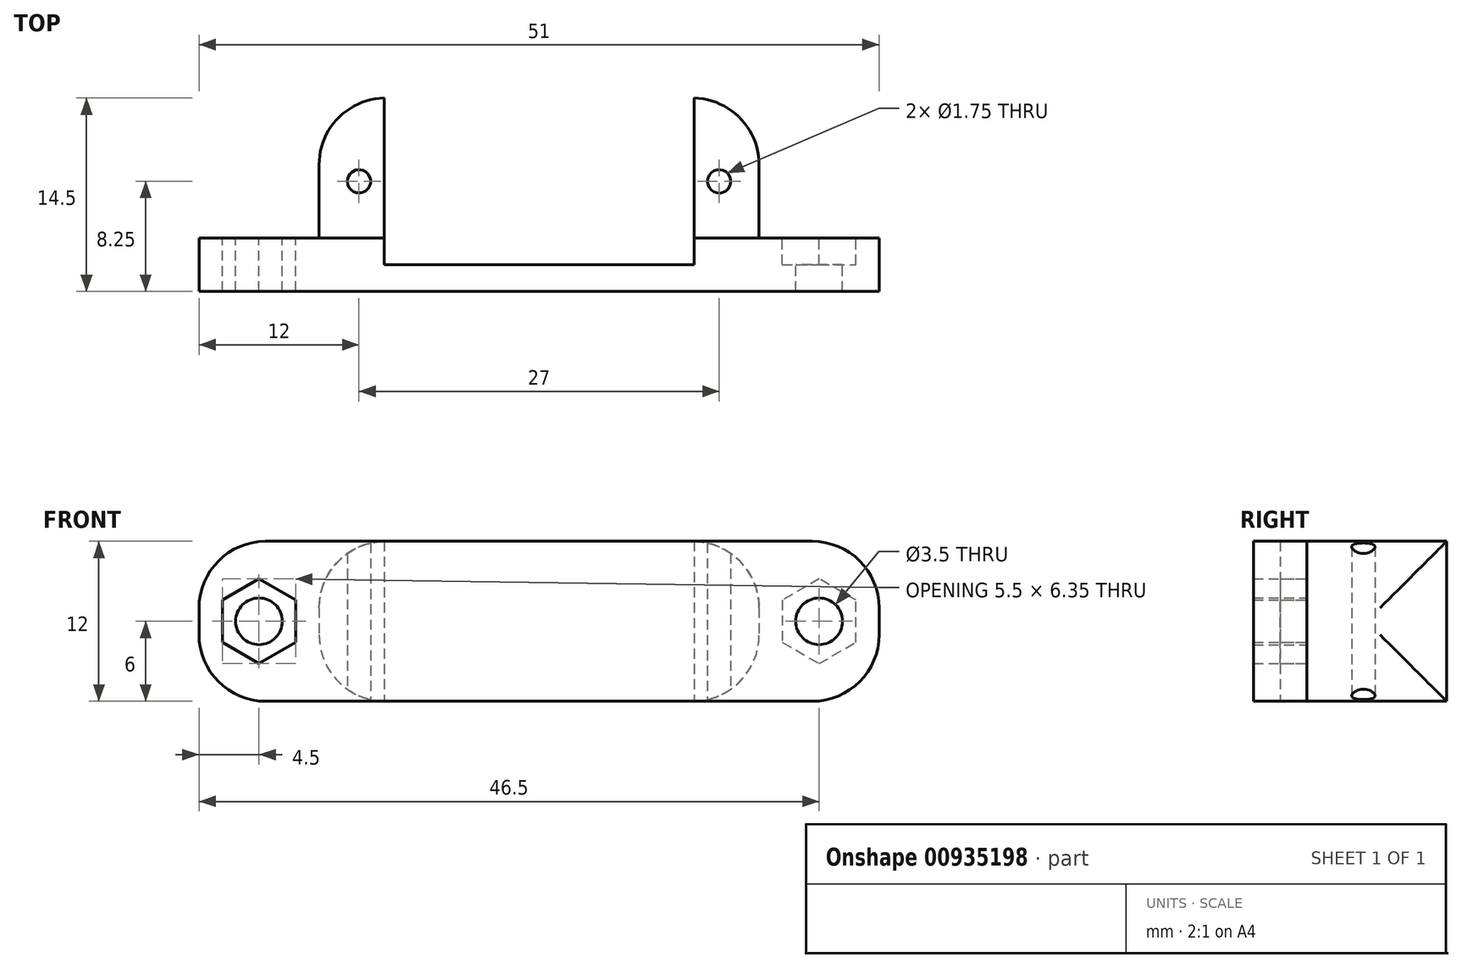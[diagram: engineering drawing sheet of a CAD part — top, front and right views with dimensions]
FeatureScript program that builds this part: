
annotation { "Feature Type Name" : "Feature", "Feature Type Description" : "" }
export const myFeature = defineFeature(function(context is Context, id is Id, definition is map)
    precondition{}
    {
        {
            var Q0;
            Q0=qCreatedBy(makeId("Top.planeOp"),FACE);
            var sketch = newSketch(context, id + "F0", { "sketchPlane" : qUnion([Q0])});
            skLineSegment(sketch, "E0.bottom", {"start": v(-16.5, 7.25) * mm, "end": v(16.5, 7.25) * mm});
            skLineSegment(sketch, "E0.top", {"start": v(-16.5, -7.25) * mm, "end": v(16.5, -7.25) * mm});
            skLineSegment(sketch, "E0.left", {"start": v(-16.5, 7.25) * mm, "end": v(-16.5, -7.25) * mm});
            skLineSegment(sketch, "E0.right", {"start": v(16.5, 7.25) * mm, "end": v(16.5, -7.25) * mm});
            skPoint(sketch, "E0.middle", {"position": v(0, 0) * mm});
            skLineSegment(sketch, "E1", {"start": v(-16.5, -5.25) * mm, "end": v(16.5, -5.25) * mm});
            skLineSegment(sketch, "E2", {"start": v(-11.63, 7.25) * mm, "end": v(-11.63, -5.25) * mm});
            skLineSegment(sketch, "E3.MirrorCS", {"start": v(11.63, 7.25) * mm, "end": v(11.63, -5.25) * mm});
            skCircle(sketch, "E4", {"center": v(-13.5, 1) * mm, "radius": 0.88 * mm});
            skCircle(sketch, "E5.MirrorC", {"center": v(13.5, 1) * mm, "radius": 0.88 * mm});
            skLineSegment(sketch, "E6.bottom", {"start": v(-16.5, -7.25) * mm, "end": v(-25.5, -7.25) * mm});
            skLineSegment(sketch, "E6.top", {"start": v(-16.5, -3.25) * mm, "end": v(-25.5, -3.25) * mm});
            skLineSegment(sketch, "E6.left", {"start": v(-16.5, -7.25) * mm, "end": v(-16.5, -3.25) * mm});
            skLineSegment(sketch, "E6.right", {"start": v(-25.5, -7.25) * mm, "end": v(-25.5, -3.25) * mm});
            skLineSegment(sketch, "E7.MirrorCS", {"start": v(16.5, -3.25) * mm, "end": v(25.5, -3.25) * mm});
            skLineSegment(sketch, "E8.MirrorCS", {"start": v(25.5, -7.25) * mm, "end": v(25.5, -3.25) * mm});
            skLineSegment(sketch, "E9.MirrorCS", {"start": v(16.5, -7.25) * mm, "end": v(25.5, -7.25) * mm});
            skSolve(sketch);
        }
        {
            var Q0;
            {var subQ3=sQuery(id+"F0.wireOp",EDGE,"E2");Q0=makeQuery(id+"F0.imprint","IMPRINT",FACE,{"disambiguationData":[TD([[makeQuery(id+"F0.imprint","IMPRINT",EDGE,{"derivedFrom":subQ3}),-1.0]])]});}
            var Q1;
            {var subQ1=sQuery(id+"F0.wireOp",EDGE,"E6.bottom");Q1=makeQuery(id+"F0.imprint","IMPRINT",FACE,{"disambiguationData":[TD([[makeQuery(id+"F0.imprint","IMPRINT",EDGE,{"derivedFrom":subQ1}),-1.0]])]});}
            var Q2;
            {var subQ1=sQuery(id+"F0.wireOp",EDGE,"E0.top");Q2=makeQuery(id+"F0.imprint","IMPRINT",FACE,{"disambiguationData":[TD([[makeQuery(id+"F0.imprint","IMPRINT",EDGE,{"derivedFrom":subQ1}),1.0]])]});}
            var Q3;
            {var subQ0=sQuery(id+"F0.wireOp",EDGE,"E7.MirrorCS");Q3=makeQuery(id+"F0.imprint","IMPRINT",FACE,{"disambiguationData":[TD([[makeQuery(id+"F0.imprint","IMPRINT",EDGE,{"derivedFrom":subQ0}),-1.0]])]});}
            var Q4;
            {var subQ4=sQuery(id+"F0.wireOp",EDGE,"E3.MirrorCS");Q4=makeQuery(id+"F0.imprint","IMPRINT",FACE,{"disambiguationData":[TD([[makeQuery(id+"F0.imprint","IMPRINT",EDGE,{"derivedFrom":subQ4}),1.0]])]});}
            extrude(context, id + "F1", {"entities" : qUnion([Q0, Q1, Q2, Q3, Q4]), "depth" : 12 * mm, "offsetDistance" : 25 * mm});
        }
        {
            var Q0;
            Q0=makeQuery(id+"F1.opExtrude","SWEPT_FACE",FACE,{"disambiguationData":[OSD([sQuery(id+"F0.wireOp",EDGE,"E7.MirrorCS")])]});
            var sketch = newSketch(context, id + "F2", { "sketchPlane" : qUnion([Q0])});
            skCircle(sketch, "E10.cCircle", {"center": v(-21, 6) * mm, "radius": 2.75 * mm, "construction": true});
            skLineSegment(sketch, "E10.0", {"start": v(-23.75, 4.41) * mm, "end": v(-23.75, 7.59) * mm});
            skLineSegment(sketch, "E10.1", {"start": v(-23.75, 7.59) * mm, "end": v(-21, 9.18) * mm});
            skLineSegment(sketch, "E10.2", {"start": v(-21, 9.18) * mm, "end": v(-18.25, 7.59) * mm});
            skLineSegment(sketch, "E10.3", {"start": v(-18.25, 7.59) * mm, "end": v(-18.25, 4.41) * mm});
            skLineSegment(sketch, "E10.4", {"start": v(-18.25, 4.41) * mm, "end": v(-21, 2.82) * mm});
            skLineSegment(sketch, "E10.5", {"start": v(-21, 2.82) * mm, "end": v(-23.75, 4.41) * mm});
            skPoint(sketch, "E10.0.midPoint", {"position": v(-23.75, 6) * mm});
            skCircle(sketch, "E11", {"center": v(-21, 6) * mm, "radius": 1.75 * mm});
            skLineSegment(sketch, "E12.MirrorCS", {"start": v(23.75, 7.59) * mm, "end": v(21, 9.18) * mm});
            skLineSegment(sketch, "E13.MirrorCS", {"start": v(21, 9.18) * mm, "end": v(18.25, 7.59) * mm});
            skLineSegment(sketch, "E14.MirrorCS", {"start": v(18.25, 4.41) * mm, "end": v(21, 2.82) * mm});
            skLineSegment(sketch, "E15.MirrorCS", {"start": v(21, 2.82) * mm, "end": v(23.75, 4.41) * mm});
            skLineSegment(sketch, "E16.MirrorCS", {"start": v(23.75, 4.41) * mm, "end": v(23.75, 7.59) * mm});
            skLineSegment(sketch, "E17.MirrorCS", {"start": v(18.25, 7.59) * mm, "end": v(18.25, 4.41) * mm});
            skCircle(sketch, "E18.MirrorC", {"center": v(21, 6) * mm, "radius": 2.75 * mm, "construction": true});
            skCircle(sketch, "E19.MirrorC", {"center": v(21, 6) * mm, "radius": 1.75 * mm});
            skPoint(sketch, "E20.MirrorP", {"position": v(23.75, 6) * mm});
            skSolve(sketch);
        }
        {
            var Q0;
            Q0=makeQuery(id+"F2.imprint","IMPRINT",FACE,{"disambiguationData":[TD([[makeQuery(id+"F2.imprint","IMPRINT",EDGE,{"derivedFrom":sQuery(id+"F2.wireOp",EDGE,"E11")}),1.0]])]});
            var Q1;
            Q1=makeQuery(id+"F2.imprint","IMPRINT",FACE,{"disambiguationData":[TD([[makeQuery(id+"F2.imprint","IMPRINT",EDGE,{"derivedFrom":sQuery(id+"F2.wireOp",EDGE,"E19.MirrorC")}),-1.0]])]});
            extrude(context, id + "F3", {"entities" : qUnion([Q0, Q1]), "operationType" : NewBodyOperationType.REMOVE, "oppositeDirection" : true, "depth" : 25 * mm, "offsetDistance" : 25 * mm});
        }
        {
            var Q0;
            Q0=makeQuery(id+"F2.imprint","IMPRINT",FACE,{"disambiguationData":[TD([[makeQuery(id+"F2.imprint","IMPRINT",EDGE,{"derivedFrom":sQuery(id+"F2.wireOp",EDGE,"E10.0")}),-1.0]])]});
            var Q1;
            Q1=makeQuery(id+"F2.imprint","IMPRINT",FACE,{"disambiguationData":[TD([[makeQuery(id+"F2.imprint","IMPRINT",EDGE,{"derivedFrom":sQuery(id+"F2.wireOp",EDGE,"E12.MirrorCS")}),1.0]])]});
            extrude(context, id + "F4", {"entities" : qUnion([Q0, Q1]), "operationType" : NewBodyOperationType.REMOVE, "oppositeDirection" : true, "depth" : 2 * mm, "offsetDistance" : 25 * mm});
        }
        {
            var Q0;
            Q0=makeQuery(id+"F1.opExtrude","SWEPT_EDGE",EDGE,{"disambiguationData":[OSD([sQuery(id+"F0.wireOp",EDGE,"E0.bottom"),sQuery(id+"F0.wireOp",EDGE,"E0.left")])]});
            var Q1;
            Q1=makeQuery(id+"F1.opExtrude","SWEPT_EDGE",EDGE,{"disambiguationData":[OSD([sQuery(id+"F0.wireOp",EDGE,"E0.bottom"),sQuery(id+"F0.wireOp",EDGE,"E0.right")])]});
            var Q2;
            Q2=makeQuery(id+"F1.opExtrude","CAP_EDGE",EDGE,{"disambiguationData":[OSD([sQuery(id+"F0.wireOp",EDGE,"E8.MirrorCS")])],"isStart":false});
            var Q3;
            Q3=makeQuery(id+"F1.opExtrude","CAP_EDGE",EDGE,{"disambiguationData":[OSD([sQuery(id+"F0.wireOp",EDGE,"E8.MirrorCS")])],"isStart":true});
            var Q4;
            Q4=makeQuery(id+"F1.opExtrude","CAP_EDGE",EDGE,{"disambiguationData":[OSD([sQuery(id+"F0.wireOp",EDGE,"E0.right")])],"isStart":true});
            var Q5;
            Q5=makeQuery(id+"F1.opExtrude","CAP_EDGE",EDGE,{"disambiguationData":[OSD([sQuery(id+"F0.wireOp",EDGE,"E0.right")])],"isStart":false});
            var Q6;
            Q6=makeQuery(id+"F1.opExtrude","CAP_EDGE",EDGE,{"disambiguationData":[OSD([sQuery(id+"F0.wireOp",EDGE,"E6.right")])],"isStart":true});
            var Q7;
            Q7=makeQuery(id+"F1.opExtrude","CAP_EDGE",EDGE,{"disambiguationData":[OSD([sQuery(id+"F0.wireOp",EDGE,"E6.right")])],"isStart":false});
            var Q8;
            Q8=makeQuery(id+"F1.opExtrude","CAP_EDGE",EDGE,{"disambiguationData":[OSD([sQuery(id+"F0.wireOp",EDGE,"E0.left")])],"isStart":false});
            var Q9;
            Q9=makeQuery(id+"F1.opExtrude","CAP_EDGE",EDGE,{"disambiguationData":[OSD([sQuery(id+"F0.wireOp",EDGE,"E0.left")])],"isStart":true});
            fillet(context, id + "F5", {"entities" : qUnion([Q0, Q1, Q2, Q3, Q4, Q5, Q6, Q7, Q8, Q9]), "radius" : 5 * mm, "tangentPropagation" : true, "allowEdgeOverflow" : false});
        }
    });
